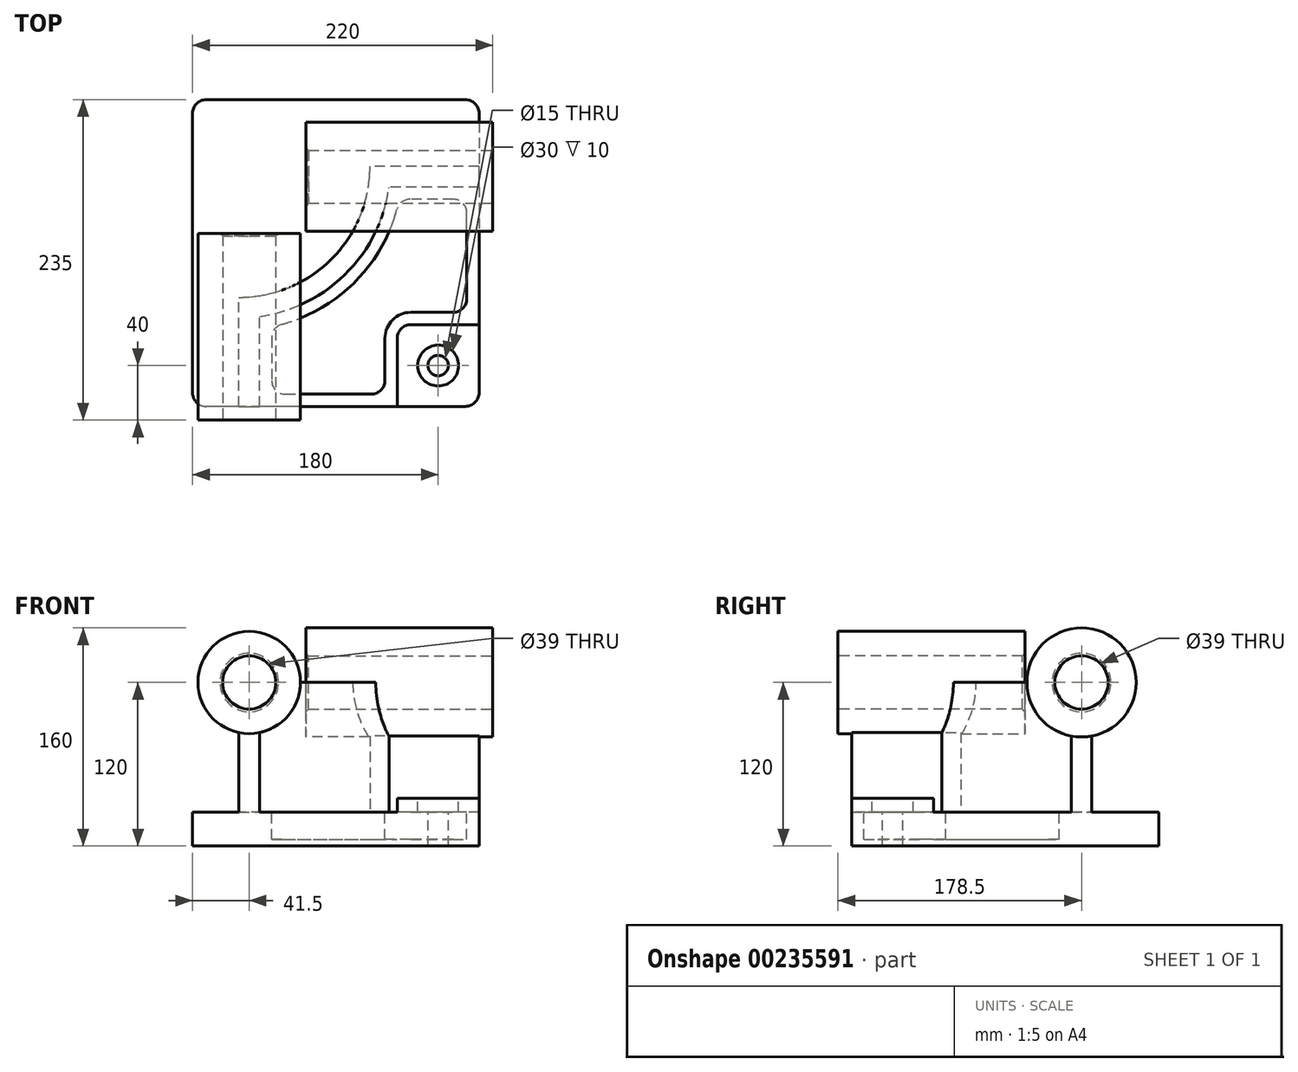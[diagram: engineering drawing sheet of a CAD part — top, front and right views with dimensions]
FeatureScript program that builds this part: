
annotation { "Feature Type Name" : "Feature", "Feature Type Description" : "" }
export const myFeature = defineFeature(function(context is Context, id is Id, definition is map)
    precondition{}
    {
        {
            var Q0;
            Q0=qCreatedBy(makeId("Top.planeOp"),FACE);
            var sketch = newSketch(context, id + "F0", { "sketchPlane" : qUnion([Q0])});
            skLineSegment(sketch, "E0.bottom", {"start": v(105, 112.5) * mm, "end": v(-105, 112.5) * mm});
            skLineSegment(sketch, "E0.top", {"start": v(105, -112.5) * mm, "end": v(-105, -112.5) * mm});
            skLineSegment(sketch, "E0.left", {"start": v(105, 112.5) * mm, "end": v(105, -112.5) * mm});
            skLineSegment(sketch, "E0.right", {"start": v(-105, 112.5) * mm, "end": v(-105, -112.5) * mm});
            skPoint(sketch, "E0.middle", {"position": v(0, 0) * mm});
            skSolve(sketch);
        }
        {
            var Q0;
            Q0=makeQuery(id+"F0.imprint","IMPRINT",FACE,{"disambiguationData":[TD([[makeQuery(id+"F0.imprint","IMPRINT",EDGE,{"derivedFrom":sQuery(id+"F0.wireOp",EDGE,"E0.bottom")}),1.0]])]});
            extrude(context, id + "F1", {"entities" : qUnion([Q0]), "depth" : 25 * mm});
        }
        {
            var Q0;
            Q0=makeQuery(id+"F1.opExtrude","CAP_FACE",FACE,{"disambiguationData":[OSD([sQuery(id+"F0.wireOp",EDGE,"E0.bottom"),sQuery(id+"F0.wireOp",EDGE,"E0.top"),sQuery(id+"F0.wireOp",EDGE,"E0.left"),sQuery(id+"F0.wireOp",EDGE,"E0.right")])],"isStart":false});
            var sketch = newSketch(context, id + "F2", { "sketchPlane" : qUnion([Q0])});
            skLineSegment(sketch, "E1", {"start": v(-71, -112.5) * mm, "end": v(-71, -32.5) * mm});
            skLineSegment(sketch, "E2", {"start": v(105, 63.5) * mm, "end": v(25, 63.5) * mm});
            skArc(sketch, "E3", {"start": v(-71, -32.5) * mm, "mid": v(-3.12, -4.38) * mm, "end": v(25, 63.5) * mm});
            skLineSegment(sketch, "E4", {"start": v(-71, 63.5) * mm, "end": v(25, 63.5) * mm, "construction": true});
            skLineSegment(sketch, "E5", {"start": v(-71, 63.5) * mm, "end": v(-71, -32.5) * mm, "construction": true});
            skLineSegment(sketch, "E6.0", {"start": v(-56, -112.5) * mm, "end": v(-56, -46.48) * mm});
            skArc(sketch, "E6.1", {"start": v(-56, -46.48) * mm, "mid": v(7.49, -14.99) * mm, "end": v(38.98, 48.5) * mm});
            skLineSegment(sketch, "E6.2", {"start": v(105, 48.5) * mm, "end": v(38.98, 48.5) * mm});
            skSolve(sketch);
        }
        {
            var Q0;
            {var subQ2=sQuery(id+"F2.wireOp",EDGE,"E1");Q0=makeQuery(id+"F2.imprint","IMPRINT",FACE,{"disambiguationData":[TD([[makeQuery(id+"F2.imprint","IMPRINT",EDGE,{"derivedFrom":subQ2}),-1.0]])]});}
            extrude(context, id + "F3", {"entities" : qUnion([Q0]), "operationType" : NewBodyOperationType.ADD, "depth" : 95 * mm});
        }
        {
            var Q0;
            {var subQ0=sQuery(id+"F0.wireOp",EDGE,"E0.left");var subQ1=sQuery(id+"F0.wireOp",EDGE,"E0.top");Q0=makeQuery(id+"F3.boolean.opBoolean","SPLIT",FACE,{"disambiguationData":[TD([makeQuery(id+"F3.opExtrude","SWEPT_FACE",FACE,{"disambiguationData":[OSD([sQuery(id+"F2.wireOp",EDGE,"E6.0")])]})])],"derivedFrom":makeQuery(id+"F1.opExtrude","CAP_FACE",FACE,{"disambiguationData":[OSD([sQuery(id+"F0.wireOp",EDGE,"E0.bottom"),subQ1,subQ0,sQuery(id+"F0.wireOp",EDGE,"E0.right")])],"isStart":false})});}
            var sketch = newSketch(context, id + "F4", { "sketchPlane" : qUnion([Q0])});
            skLineSegment(sketch, "E7.bottom", {"start": v(105, -112.5) * mm, "end": v(45, -112.5) * mm});
            skLineSegment(sketch, "E7.top", {"start": v(105, -52.5) * mm, "end": v(45, -52.5) * mm});
            skLineSegment(sketch, "E7.left", {"start": v(105, -112.5) * mm, "end": v(105, -52.5) * mm});
            skLineSegment(sketch, "E7.right", {"start": v(45, -112.5) * mm, "end": v(45, -52.5) * mm});
            skSolve(sketch);
        }
        {
            var Q0;
            {var subQ0=sQuery(id+"F0.wireOp",EDGE,"E0.top");Q0=makeQuery(id+"F3.boolean.opBoolean","MERGE",FACE,{"derivedFrom":[makeQuery(id+"F1.opExtrude","SWEPT_FACE",FACE,{"disambiguationData":[OSD([subQ0])]}),makeQuery(id+"F3.opExtrude","SWEPT_FACE",FACE,{"disambiguationData":[OSD([subQ0])]})]});}
            var sketch = newSketch(context, id + "F5", { "sketchPlane" : qUnion([Q0])});
            skCircle(sketch, "E8", {"center": v(-63.5, 120) * mm, "radius": 37.5 * mm});
            skSolve(sketch);
        }
        {
            var Q0;
            Q0 = qSketchRegion(id + "F5", true);
            extrude(context, id + "F6", {"entities" : qUnion([Q0]), "operationType" : NewBodyOperationType.ADD, "depth" : 10 * mm, "hasSecondDirection" : true, "secondDirectionOppositeDirection" : true, "secondDirectionDepth" : 127 * mm});
        }
        {
            var Q0;
            {var subQ0=sQuery(id+"F0.wireOp",EDGE,"E0.left");Q0=makeQuery(id+"F3.boolean.opBoolean","MERGE",FACE,{"derivedFrom":[makeQuery(id+"F1.opExtrude","SWEPT_FACE",FACE,{"disambiguationData":[OSD([subQ0])]}),makeQuery(id+"F3.opExtrude","SWEPT_FACE",FACE,{"disambiguationData":[OSD([subQ0])]})]});}
            var sketch = newSketch(context, id + "F7", { "sketchPlane" : qUnion([Q0])});
            skCircle(sketch, "E9", {"center": v(56, 120) * mm, "radius": 40 * mm});
            skSolve(sketch);
        }
        {
            var Q0;
            Q0 = qSketchRegion(id + "F7", true);
            extrude(context, id + "F8", {"entities" : qUnion([Q0]), "operationType" : NewBodyOperationType.ADD, "depth" : 10 * mm, "hasSecondDirection" : true, "secondDirectionOppositeDirection" : true, "secondDirectionDepth" : 127 * mm});
        }
        {
            var Q0;
            Q0 = qSketchRegion(id + "F4", true);
            extrude(context, id + "F9", {"entities" : qUnion([Q0]), "operationType" : NewBodyOperationType.ADD, "depth" : 10 * mm});
        }
        {
            var Q0;
            Q0=makeQuery(id+"F9.opExtrude","SWEPT_EDGE",EDGE,{"disambiguationData":[OSD([sQuery(id+"F4.wireOp",EDGE,"E7.top"),sQuery(id+"F4.wireOp",EDGE,"E7.right")])]});
            fillet(context, id + "F10", {"entities" : qUnion([Q0]), "radius" : 10 * mm, "tangentPropagation" : true, "allowEdgeOverflow" : false});
        }
        {
            var Q0;
            {var subQ0=sQuery(id+"F0.wireOp",EDGE,"E0.left");var subQ1=sQuery(id+"F0.wireOp",EDGE,"E0.top");Q0=makeQuery(id+"F3.boolean.opBoolean","SPLIT",FACE,{"disambiguationData":[TD([makeQuery(id+"F3.opExtrude","SWEPT_FACE",FACE,{"disambiguationData":[OSD([sQuery(id+"F2.wireOp",EDGE,"E6.0")])]})])],"derivedFrom":makeQuery(id+"F1.opExtrude","CAP_FACE",FACE,{"disambiguationData":[OSD([sQuery(id+"F0.wireOp",EDGE,"E0.bottom"),subQ1,subQ0,sQuery(id+"F0.wireOp",EDGE,"E0.right")])],"isStart":false})});}
            var sketch = newSketch(context, id + "F11", { "sketchPlane" : qUnion([Q0])});
            skLineSegment(sketch, "E10.0", {"start": v(-47, -54.08) * mm, "end": v(-47, -103.5) * mm});
            skArc(sketch, "E10.1", {"start": v(46.58, 39.5) * mm, "mid": v(13.85, -21.35) * mm, "end": v(-47, -54.08) * mm});
            skLineSegment(sketch, "E10.2", {"start": v(-47, -103.5) * mm, "end": v(36, -103.5) * mm});
            skLineSegment(sketch, "E10.3", {"start": v(96, 39.5) * mm, "end": v(46.58, 39.5) * mm});
            skLineSegment(sketch, "E10.4", {"start": v(36, -103.5) * mm, "end": v(36, -62.5) * mm});
            skArc(sketch, "E10.5", {"start": v(36, -62.5) * mm, "mid": v(41.56, -49.06) * mm, "end": v(55, -43.5) * mm});
            skLineSegment(sketch, "E10.6", {"start": v(55, -43.5) * mm, "end": v(96, -43.5) * mm});
            skLineSegment(sketch, "E10.7", {"start": v(96, -43.5) * mm, "end": v(96, 39.5) * mm});
            skSolve(sketch);
        }
        {
            var Q0;
            Q0=makeQuery(id+"F11.imprint","IMPRINT",FACE,{"disambiguationData":[TD([[makeQuery(id+"F11.imprint","IMPRINT",EDGE,{"derivedFrom":sQuery(id+"F11.wireOp",EDGE,"E10.0")}),1.0]])]});
            extrude(context, id + "F12", {"entities" : qUnion([Q0]), "operationType" : NewBodyOperationType.REMOVE, "oppositeDirection" : true, "depth" : 20 * mm});
        }
        {
            var Q0;
            Q0=makeQuery(id+"F9.opExtrude","CAP_FACE",FACE,{"disambiguationData":[OSD([sQuery(id+"F4.wireOp",EDGE,"E7.bottom"),sQuery(id+"F4.wireOp",EDGE,"E7.top"),sQuery(id+"F4.wireOp",EDGE,"E7.left"),sQuery(id+"F4.wireOp",EDGE,"E7.right")])],"isStart":false});
            var sketch = newSketch(context, id + "F13", { "sketchPlane" : qUnion([Q0])});
            skCircle(sketch, "E11", {"center": v(75, -82.5) * mm, "radius": 15 * mm});
            skSolve(sketch);
        }
        {
            var Q0;
            Q0=sQuery(id+"F13.wireOp",VERTEX,"E11.center");
            var Q1;
            Q1=makeQuery(id+"F1.opExtrude","SWEPT_BODY",BODY,{"disambiguationData":[OSD([sQuery(id+"F0.wireOp",EDGE,"E0.bottom"),sQuery(id+"F0.wireOp",EDGE,"E0.top"),sQuery(id+"F0.wireOp",EDGE,"E0.left"),sQuery(id+"F0.wireOp",EDGE,"E0.right")])]});
            hole(context, id + "F14", {"style" : HoleStyle.C_BORE, "endStyle" : HoleEndStyle.THROUGH, "holeDiameter" : 15 * mm, "cBoreDiameter" : 30 * mm, "cBoreDepth" : 10 * mm, "locations" : qUnion([Q0]), "scope" : qUnion([Q1]), "isTappedThrough" : true});
        }
        {
            var Q0;
            Q0=makeQuery(id+"F12.boolean.opBoolean","COPY",EDGE,{"derivedFrom":makeQuery(id+"F12.opExtrude","SWEPT_EDGE",EDGE,{"disambiguationData":[OSD([sQuery(id+"F11.wireOp",EDGE,"E10.0"),sQuery(id+"F11.wireOp",EDGE,"E10.1")])]})});
            var Q1;
            Q1=makeQuery(id+"F12.boolean.opBoolean","COPY",EDGE,{"derivedFrom":makeQuery(id+"F12.opExtrude","SWEPT_EDGE",EDGE,{"disambiguationData":[OSD([sQuery(id+"F11.wireOp",EDGE,"E10.1"),sQuery(id+"F11.wireOp",EDGE,"E10.3")])]})});
            var Q2;
            Q2=makeQuery(id+"F12.boolean.opBoolean","COPY",EDGE,{"derivedFrom":makeQuery(id+"F12.opExtrude","SWEPT_EDGE",EDGE,{"disambiguationData":[OSD([sQuery(id+"F11.wireOp",EDGE,"E10.3"),sQuery(id+"F11.wireOp",EDGE,"E10.7")])]})});
            var Q3;
            Q3=makeQuery(id+"F12.boolean.opBoolean","COPY",EDGE,{"derivedFrom":makeQuery(id+"F12.opExtrude","SWEPT_EDGE",EDGE,{"disambiguationData":[OSD([sQuery(id+"F11.wireOp",EDGE,"E10.6"),sQuery(id+"F11.wireOp",EDGE,"E10.7")])]})});
            var Q4;
            Q4=makeQuery(id+"F12.boolean.opBoolean","COPY",EDGE,{"derivedFrom":makeQuery(id+"F12.opExtrude","SWEPT_EDGE",EDGE,{"disambiguationData":[OSD([sQuery(id+"F11.wireOp",EDGE,"E10.0"),sQuery(id+"F11.wireOp",EDGE,"E10.2")])]})});
            var Q5;
            Q5=makeQuery(id+"F12.boolean.opBoolean","COPY",EDGE,{"derivedFrom":makeQuery(id+"F12.opExtrude","SWEPT_EDGE",EDGE,{"disambiguationData":[OSD([sQuery(id+"F11.wireOp",EDGE,"E10.2"),sQuery(id+"F11.wireOp",EDGE,"E10.4")])]})});
            fillet(context, id + "F15", {"entities" : qUnion([Q0, Q1, Q2, Q3, Q4, Q5]), "radius" : 10 * mm, "tangentPropagation" : true, "allowEdgeOverflow" : false});
        }
        {
            var Q0;
            Q0=makeQuery(id+"F6.opExtrude","CAP_FACE",FACE,{"disambiguationData":[OSD([sQuery(id+"F5.wireOp",EDGE,"E8")])],"isStart":false});
            var sketch = newSketch(context, id + "F16", { "sketchPlane" : qUnion([Q0])});
            skCircle(sketch, "E12", {"center": v(-63.5, 120) * mm, "radius": 19.5 * mm});
            skSolve(sketch);
        }
        {
            var Q0;
            Q0 = qSketchRegion(id + "F16", true);
            extrude(context, id + "F17", {"entities" : qUnion([Q0]), "operationType" : NewBodyOperationType.REMOVE, "endBound" : BoundingType.THROUGH_ALL, "oppositeDirection" : true, "depth" : 100 * mm});
        }
        {
            var Q0;
            Q0=makeQuery(id+"F8.opExtrude","CAP_FACE",FACE,{"disambiguationData":[OSD([sQuery(id+"F7.wireOp",EDGE,"E9")])],"isStart":false});
            var sketch = newSketch(context, id + "F18", { "sketchPlane" : qUnion([Q0])});
            skCircle(sketch, "E13", {"center": v(56, 120) * mm, "radius": 19.5 * mm});
            skSolve(sketch);
        }
        {
            var Q0;
            Q0 = qSketchRegion(id + "F18", true);
            extrude(context, id + "F19", {"entities" : qUnion([Q0]), "operationType" : NewBodyOperationType.REMOVE, "endBound" : BoundingType.THROUGH_ALL, "oppositeDirection" : true, "depth" : 25 * mm});
        }
        {
            var Q0;
            Q0=makeQuery(id+"F17.boolean.opBoolean","COPY",EDGE,{"derivedFrom":makeQuery(id+"F17.opExtrude","CAP_EDGE",EDGE,{"disambiguationData":[OSD([sQuery(id+"F16.wireOp",EDGE,"E12")])],"isStart":true})});
            var Q1;
            Q1=makeQuery(id+"F19.boolean.opBoolean","COPY",EDGE,{"derivedFrom":makeQuery(id+"F19.opExtrude","CAP_EDGE",EDGE,{"disambiguationData":[OSD([sQuery(id+"F18.wireOp",EDGE,"E13")])],"isStart":true})});
            var Q2;
            Q2=makeQuery(id+"F19.boolean.opBoolean","INTERSECT",EDGE,{"derivedFrom":[makeQuery(id+"F8.opExtrude","CAP_FACE",FACE,{"disambiguationData":[OSD([sQuery(id+"F7.wireOp",EDGE,"E9")])],"isStart":true}),makeQuery(id+"F19.opExtrude","SWEPT_FACE",FACE,{"disambiguationData":[OSD([sQuery(id+"F18.wireOp",EDGE,"E13")])]})]});
            var Q3;
            Q3=makeQuery(id+"F17.boolean.opBoolean","INTERSECT",EDGE,{"derivedFrom":[makeQuery(id+"F6.opExtrude","CAP_FACE",FACE,{"disambiguationData":[OSD([sQuery(id+"F5.wireOp",EDGE,"E8")])],"isStart":true}),makeQuery(id+"F17.opExtrude","SWEPT_FACE",FACE,{"disambiguationData":[OSD([sQuery(id+"F16.wireOp",EDGE,"E12")])]})]});
            chamfer(context, id + "F20", {"entities" : qUnion([Q0, Q1, Q2, Q3]), "width" : 2 * mm, "tangentPropagation" : true});
        }
        {
            var Q0;
            Q0=makeQuery(id+"F9.boolean.opBoolean","MERGE",EDGE,{"derivedFrom":[makeQuery(id+"F1.opExtrude","SWEPT_EDGE",EDGE,{"disambiguationData":[OSD([sQuery(id+"F0.wireOp",EDGE,"E0.top"),sQuery(id+"F0.wireOp",EDGE,"E0.left")])]}),makeQuery(id+"F9.opExtrude","SWEPT_EDGE",EDGE,{"disambiguationData":[OSD([sQuery(id+"F4.wireOp",EDGE,"E7.bottom"),sQuery(id+"F4.wireOp",EDGE,"E7.left")])]})]});
            var Q1;
            Q1=makeQuery(id+"F1.opExtrude","SWEPT_EDGE",EDGE,{"disambiguationData":[OSD([sQuery(id+"F0.wireOp",EDGE,"E0.top"),sQuery(id+"F0.wireOp",EDGE,"E0.right")])]});
            var Q2;
            Q2=makeQuery(id+"F1.opExtrude","SWEPT_EDGE",EDGE,{"disambiguationData":[OSD([sQuery(id+"F0.wireOp",EDGE,"E0.bottom"),sQuery(id+"F0.wireOp",EDGE,"E0.left")])]});
            var Q3;
            Q3=makeQuery(id+"F1.opExtrude","SWEPT_EDGE",EDGE,{"disambiguationData":[OSD([sQuery(id+"F0.wireOp",EDGE,"E0.bottom"),sQuery(id+"F0.wireOp",EDGE,"E0.right")])]});
            fillet(context, id + "F21", {"entities" : qUnion([Q0, Q1, Q2, Q3]), "radius" : 10 * mm, "tangentPropagation" : true, "allowEdgeOverflow" : false});
        }
    });
